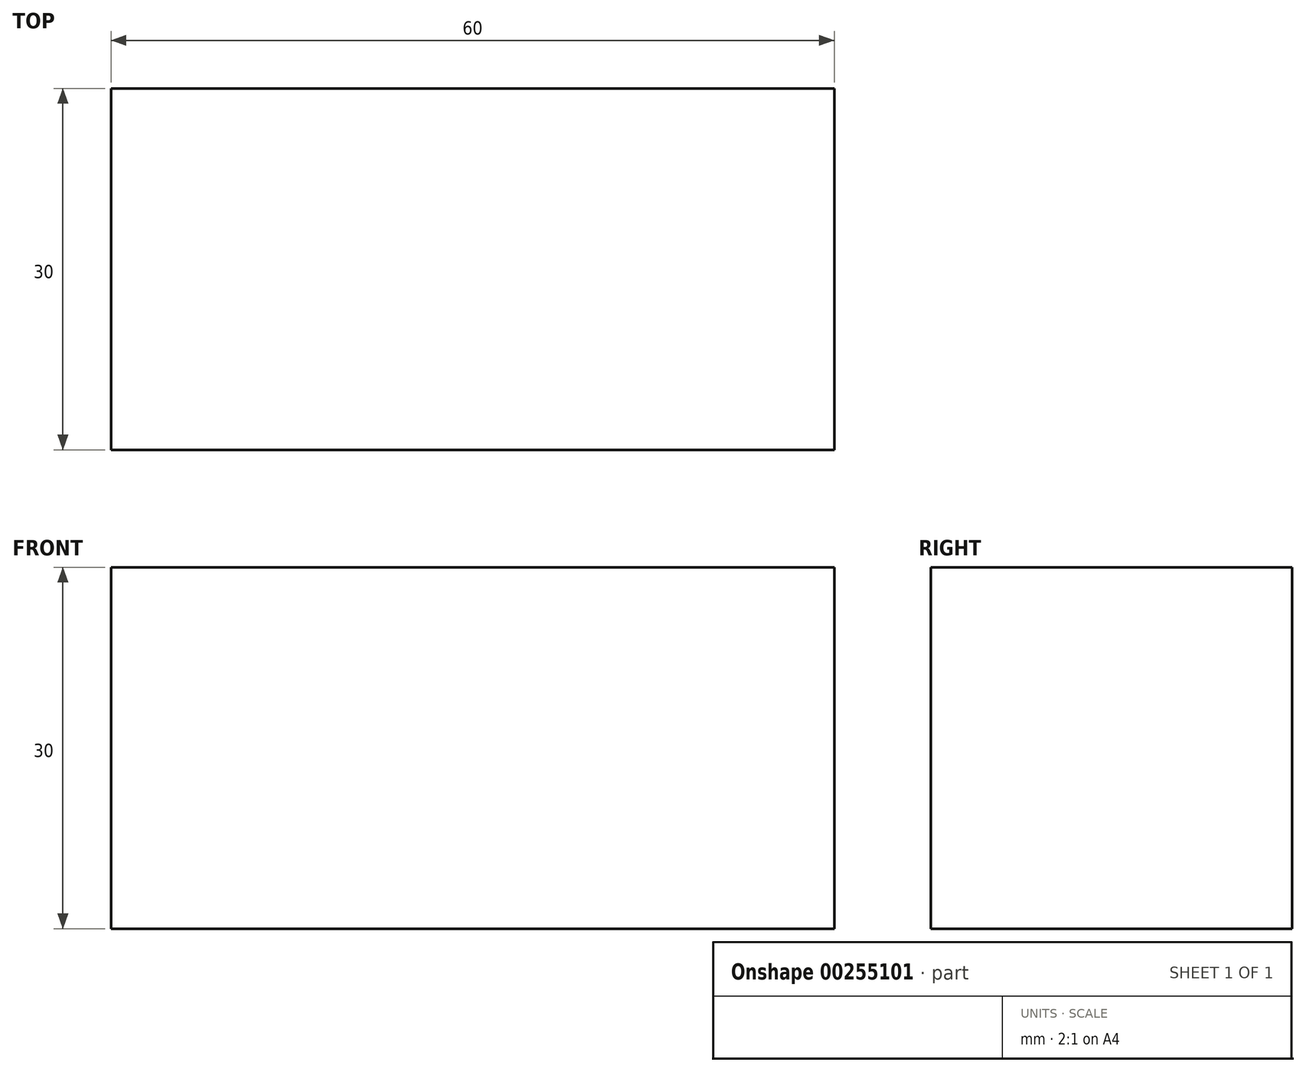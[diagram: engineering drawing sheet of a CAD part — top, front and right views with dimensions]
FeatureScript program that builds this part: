
annotation { "Feature Type Name" : "Feature", "Feature Type Description" : "" }
export const myFeature = defineFeature(function(context is Context, id is Id, definition is map)
    precondition{}
    {
        {
            var Q0;
            Q0=qCreatedBy(makeId("Front.planeOp"),FACE);
            var sketch = newSketch(context, id + "F0", { "sketchPlane" : qUnion([Q0])});
            skLineSegment(sketch, "E0.bottom", {"start": v(0, 0) * mm, "end": v(60, 0) * mm});
            skLineSegment(sketch, "E0.top", {"start": v(0, -30) * mm, "end": v(60, -30) * mm});
            skLineSegment(sketch, "E0.left", {"start": v(0, 0) * mm, "end": v(0, -30) * mm});
            skLineSegment(sketch, "E0.right", {"start": v(60, 0) * mm, "end": v(60, -30) * mm});
            skSolve(sketch);
        }
        {
            var Q0;
            Q0=makeQuery(id+"F0.imprint","IMPRINT",FACE,{"disambiguationData":[TD([[makeQuery(id+"F0.imprint","IMPRINT",EDGE,{"derivedFrom":sQuery(id+"F0.wireOp",EDGE,"E0.bottom")}),-1.0]])]});
            extrude(context, id + "F1", {"entities" : qUnion([Q0]), "depth" : 30 * mm});
        }
    });
